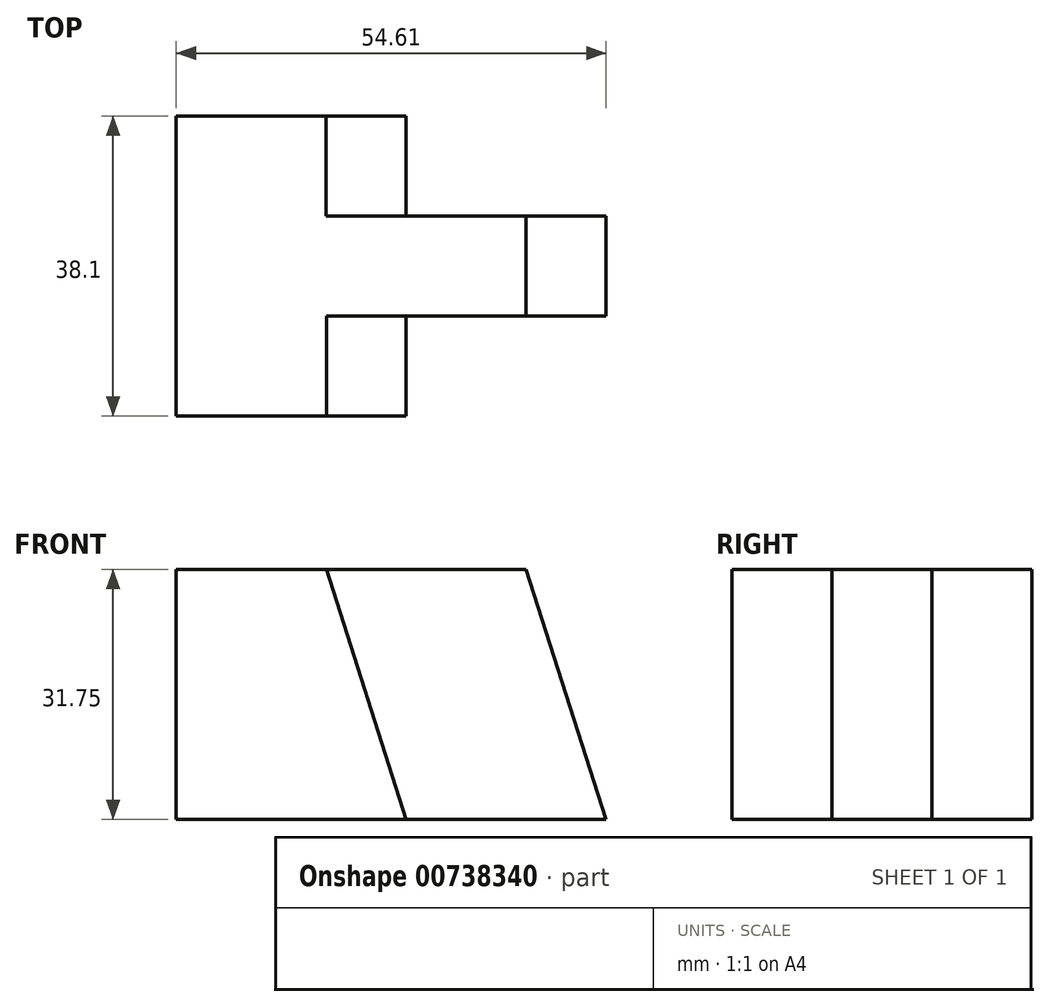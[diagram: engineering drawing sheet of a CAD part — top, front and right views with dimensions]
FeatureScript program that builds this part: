
annotation { "Feature Type Name" : "Feature", "Feature Type Description" : "" }
export const myFeature = defineFeature(function(context is Context, id is Id, definition is map)
    precondition{}
    {
        {
            var Q0;
            Q0=qCreatedBy(makeId("Front.planeOp"),FACE);
            var sketch = newSketch(context, id + "F0", { "sketchPlane" : qUnion([Q0])});
            skLineSegment(sketch, "E0", {"start": v(0, 0) * mm, "end": v(0, 31.75) * mm});
            skLineSegment(sketch, "E1", {"start": v(0, 31.75) * mm, "end": v(44.45, 31.75) * mm});
            skLineSegment(sketch, "E2", {"start": v(44.45, 31.75) * mm, "end": v(54.6, 0) * mm});
            skLineSegment(sketch, "E3", {"start": v(54.61, 0) * mm, "end": v(0, 0) * mm});
            skSolve(sketch);
        }
        {
            var Q0;
            Q0 = qSketchRegion(id + "F0", true);
            extrude(context, id + "F1", {"entities" : qUnion([Q0]), "depth" : 38.1 * mm, "offsetDistance" : 25.4 * mm});
        }
        {
            var Q0;
            Q0=makeQuery(id+"F1.opExtrude","CAP_FACE",FACE,{"disambiguationData":[OSD([sQuery(id+"F0.wireOp",EDGE,"E0"),sQuery(id+"F0.wireOp",EDGE,"E1"),sQuery(id+"F0.wireOp",EDGE,"E2"),sQuery(id+"F0.wireOp",EDGE,"E3")])],"isStart":true});
            var sketch = newSketch(context, id + "F2", { "sketchPlane" : qUnion([Q0])});
            skLineSegment(sketch, "E4", {"start": v(19.7, 31.67) * mm, "end": v(28.26, -0.05) * mm});
            skLineSegment(sketch, "E5", {"start": v(28.26, -0.05) * mm, "end": v(54.68, -0.05) * mm});
            skLineSegment(sketch, "E6", {"start": v(54.68, -0.05) * mm, "end": v(44.42, 31.67) * mm});
            skLineSegment(sketch, "E7", {"start": v(44.42, 31.67) * mm, "end": v(19.7, 31.67) * mm});
            skLineSegment(sketch, "E8", {"start": v(-54.6, 0) * mm, "end": v(-29.17, 0) * mm});
            skLineSegment(sketch, "E9", {"start": v(-29.17, 0) * mm, "end": v(-19.05, 31.75) * mm});
            skLineSegment(sketch, "E10", {"start": v(-19.05, 31.75) * mm, "end": v(-44.45, 31.75) * mm});
            skLineSegment(sketch, "E11", {"start": v(-44.45, 31.75) * mm, "end": v(-54.61, 0) * mm});
            skSolve(sketch);
        }
        {
            var Q0;
            Q0 = qSketchRegion(id + "F2", true);
            extrude(context, id + "F3", {"entities" : qUnion([Q0]), "operationType" : NewBodyOperationType.REMOVE, "oppositeDirection" : true, "depth" : 12.7 * mm, "offsetDistance" : 25.4 * mm});
        }
        {
            var Q0;
            Q0 = qSketchRegion(id + "F2", true);
            extrude(context, id + "F4", {"entities" : qUnion([Q0]), "operationType" : NewBodyOperationType.REMOVE, "oppositeDirection" : true, "depth" : 12.7 * mm, "offsetDistance" : 25.4 * mm});
        }
        {
            var Q0;
            Q0=makeQuery(id+"F1.opExtrude","CAP_FACE",FACE,{"disambiguationData":[OSD([sQuery(id+"F0.wireOp",EDGE,"E0"),sQuery(id+"F0.wireOp",EDGE,"E1"),sQuery(id+"F0.wireOp",EDGE,"E2"),sQuery(id+"F0.wireOp",EDGE,"E3")])],"isStart":false});
            var sketch = newSketch(context, id + "F5", { "sketchPlane" : qUnion([Q0])});
            skLineSegment(sketch, "E12", {"start": v(54.6, 0) * mm, "end": v(29.21, 0) * mm});
            skLineSegment(sketch, "E13", {"start": v(29.21, 0) * mm, "end": v(19.09, 31.75) * mm});
            skLineSegment(sketch, "E14", {"start": v(19.09, 31.75) * mm, "end": v(44.45, 31.75) * mm});
            skLineSegment(sketch, "E15", {"start": v(44.45, 31.75) * mm, "end": v(54.61, 0) * mm});
            skSolve(sketch);
        }
        {
            var Q0;
            Q0 = qSketchRegion(id + "F5", true);
            extrude(context, id + "F6", {"entities" : qUnion([Q0]), "operationType" : NewBodyOperationType.REMOVE, "oppositeDirection" : true, "depth" : 12.7 * mm, "offsetDistance" : 25.4 * mm});
        }
    });
